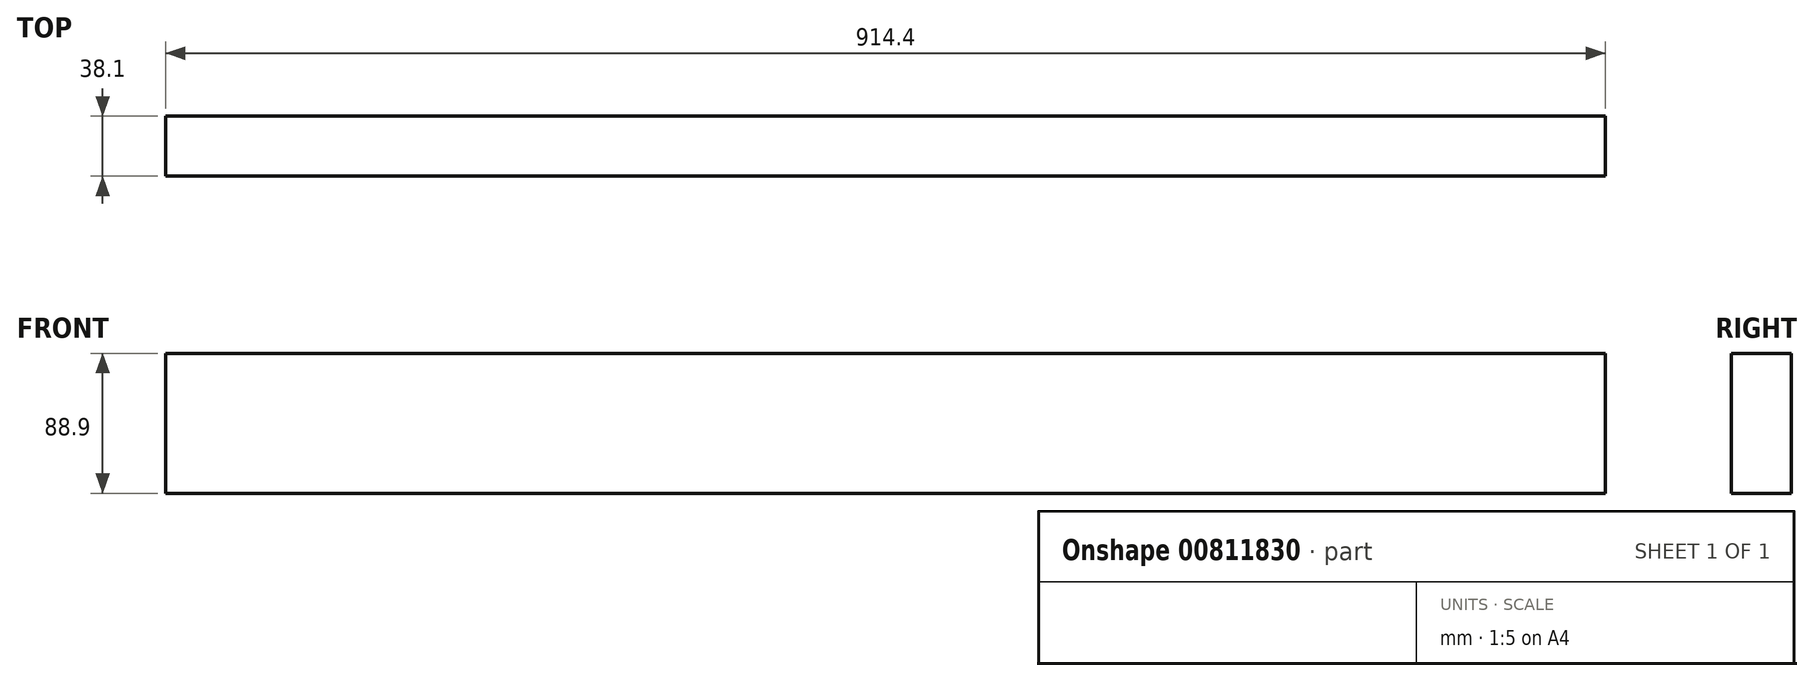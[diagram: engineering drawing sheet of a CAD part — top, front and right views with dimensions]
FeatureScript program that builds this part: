
annotation { "Feature Type Name" : "Feature", "Feature Type Description" : "" }
export const myFeature = defineFeature(function(context is Context, id is Id, definition is map)
    precondition{}
    {
        {
            var Q0;
            Q0=qCreatedBy(makeId("Front.planeOp"),FACE);
            var sketch = newSketch(context, id + "F0", { "sketchPlane" : qUnion([Q0])});
            skLineSegment(sketch, "E0.bottom", {"start": v(-433.1, 88.9) * mm, "end": v(481.3, 88.9) * mm});
            skLineSegment(sketch, "E0.top", {"start": v(-433.1, 0) * mm, "end": v(481.3, 0) * mm});
            skLineSegment(sketch, "E0.left", {"start": v(-433.1, 88.9) * mm, "end": v(-433.1, 0) * mm});
            skLineSegment(sketch, "E0.right", {"start": v(481.3, 88.9) * mm, "end": v(481.3, 0) * mm});
            skSolve(sketch);
        }
        {
            var Q0;
            Q0 = qSketchRegion(id + "F0", true);
            extrude(context, id + "F1", {"entities" : qUnion([Q0]), "endBound" : BoundingType.SYMMETRIC, "depth" : 38.1 * mm, "offsetDistance" : 25.4 * mm});
        }
    });
